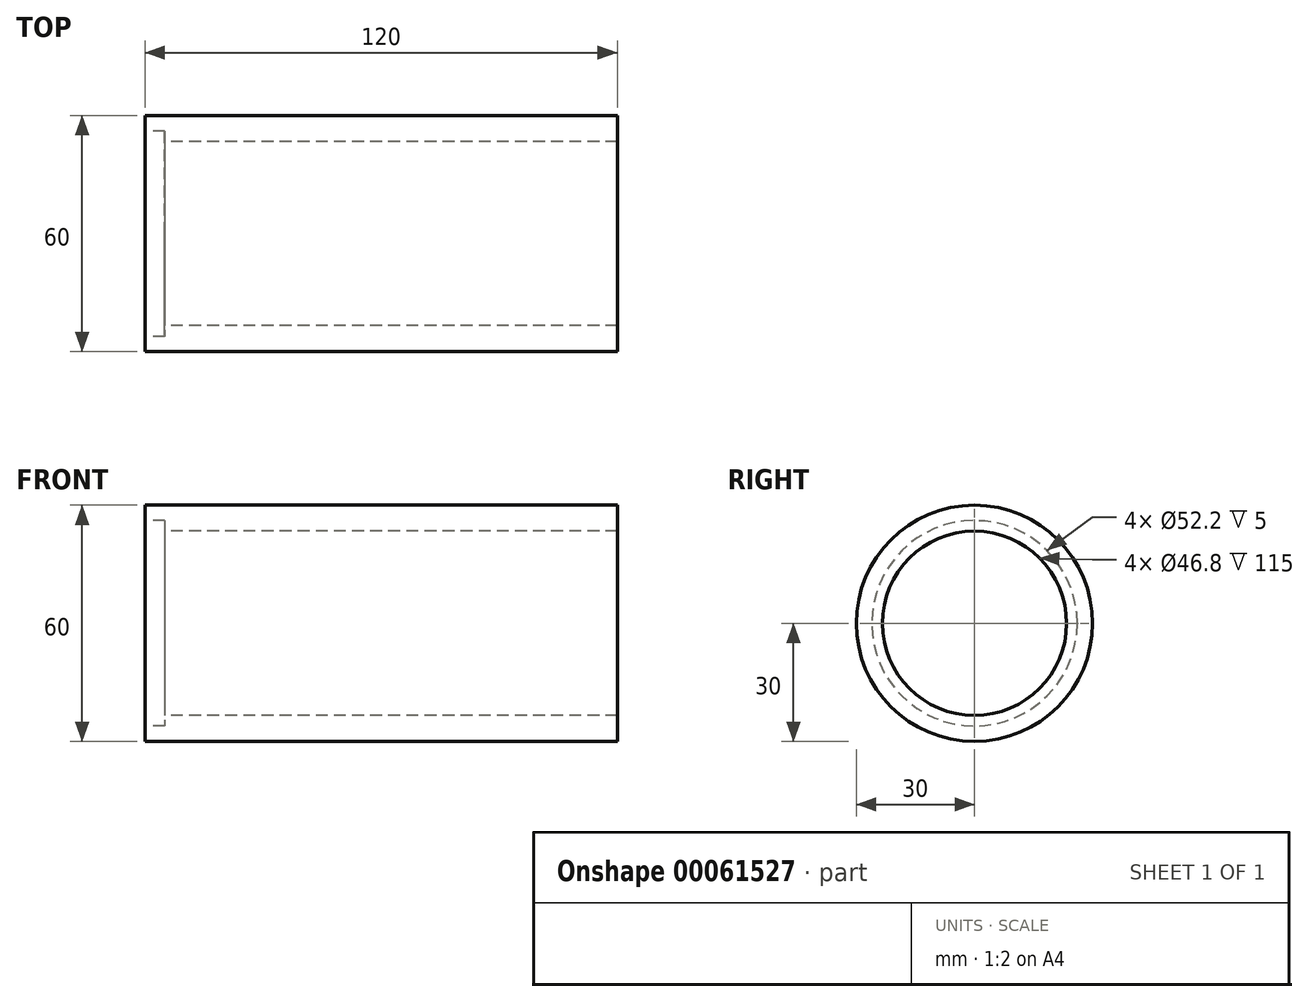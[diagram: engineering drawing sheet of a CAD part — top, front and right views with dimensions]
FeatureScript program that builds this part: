
annotation { "Feature Type Name" : "Feature", "Feature Type Description" : "" }
export const myFeature = defineFeature(function(context is Context, id is Id, definition is map)
    precondition{}
    {
        {
            var Q0;
            Q0=qCreatedBy(makeId("Front.planeOp"),FACE);
            var sketch = newSketch(context, id + "F0", { "sketchPlane" : qUnion([Q0])});
            skLineSegment(sketch, "E0", {"start": v(0, 30) * mm, "end": v(120, 30) * mm});
            skLineSegment(sketch, "E1", {"start": v(120, 30) * mm, "end": v(120, 23.4) * mm});
            skLineSegment(sketch, "E2", {"start": v(120, 23.4) * mm, "end": v(5, 23.4) * mm});
            skLineSegment(sketch, "E3", {"start": v(5, 23.4) * mm, "end": v(5, 26.1) * mm});
            skLineSegment(sketch, "E4", {"start": v(5, 26.1) * mm, "end": v(0, 26.1) * mm});
            skLineSegment(sketch, "E5", {"start": v(0, 26.1) * mm, "end": v(0, 30) * mm});
            skLineSegment(sketch, "E6", {"start": v(0, 0) * mm, "end": v(120, 0) * mm});
            skSolve(sketch);
        }
        {
            var Q0;
            Q0=makeQuery(id+"F0.imprint","IMPRINT",FACE,{"disambiguationData":[TD([[makeQuery(id+"F0.imprint","IMPRINT",EDGE,{"derivedFrom":sQuery(id+"F0.wireOp",EDGE,"E0")}),-1.0]])]});
            var Q1;
            Q1=sQuery(id+"F0.wireOp",EDGE,"E6");
            revolve(context, id + "F1", {"entities" : qUnion([Q0]), "axis" : qUnion([Q1]), "revolveType" : RevolveType.FULL});
        }
    });
